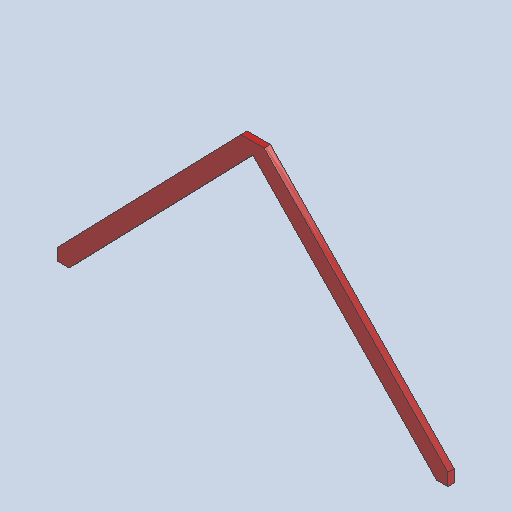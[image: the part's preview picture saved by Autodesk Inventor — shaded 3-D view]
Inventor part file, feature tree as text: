
AUTODESK INVENTOR PART (.ipt)
format: ipt  version: 2025.1 (Build 291241020, 241B)  size: 262,144 bytes
history: native  units: in
note: dims shown in document units (in); Inventor stores cm internally (conversion verified against a paired STEP export)
features: other x7, reference x4, extrude x1, sketch x1
ambient origin geometry x8: Origin, YZ Plane, XZ Plane, XY Plane, X Axis, Y Axis, Z Axis, Center Point
bodies: Solid1 (feature_tree)
feature tree (13):
  extrude  "Extrusion1"  [1 undecoded]
  sketch  "Sketch1"  dims[d0=1.5in d1=0.0in]
  reference  "Reference1"
  reference  "Reference2"
  reference  "Reference3"
  reference  "Reference4"
  other  "<userpath>\Documents\Tburn24\B_Legs0\B_Legs0.iam"
  other  "B_Legs0.iam"
  other  "8'x2x4:4"
  other  "4x2x4:3"
  other  "8'x2x4:2"
  other  "4x2x4:2"
  other  "Finish1"
note: 1 required parameter value undecoded (feature->parameter linkage not recoverable at this tier; creation-order binding heuristic only, values carry confidence <= 0.55)
